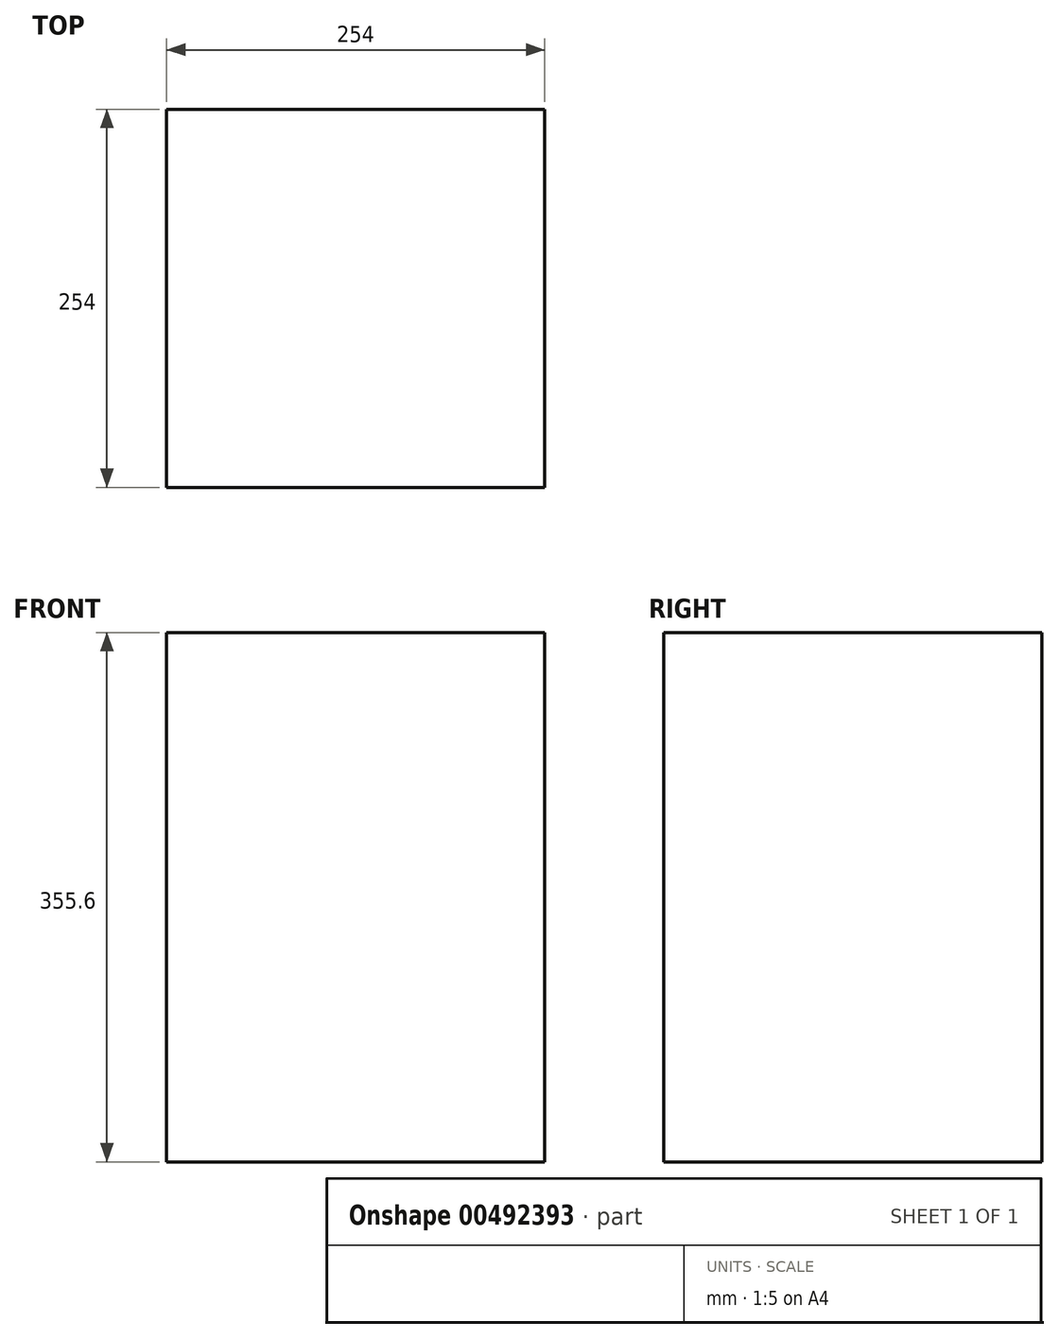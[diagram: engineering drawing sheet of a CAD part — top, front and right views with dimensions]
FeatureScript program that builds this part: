
annotation { "Feature Type Name" : "Feature", "Feature Type Description" : "" }
export const myFeature = defineFeature(function(context is Context, id is Id, definition is map)
    precondition{}
    {
        {
            var Q0;
            Q0=qCreatedBy(makeId("Top.planeOp"),FACE);
            var sketch = newSketch(context, id + "F0", { "sketchPlane" : qUnion([Q0])});
            skLineSegment(sketch, "E0.bottom", {"start": v(127, 127) * mm, "end": v(-127, 127) * mm});
            skLineSegment(sketch, "E0.top", {"start": v(127, -127) * mm, "end": v(-127, -127) * mm});
            skLineSegment(sketch, "E0.left", {"start": v(127, 127) * mm, "end": v(127, -127) * mm});
            skLineSegment(sketch, "E0.right", {"start": v(-127, 127) * mm, "end": v(-127, -127) * mm});
            skPoint(sketch, "E0.middle", {"position": v(0, 0) * mm});
            skSolve(sketch);
        }
        {
            var Q0;
            Q0=makeQuery(id+"F0.imprint","IMPRINT",FACE,{"disambiguationData":[TD([[makeQuery(id+"F0.imprint","IMPRINT",EDGE,{"derivedFrom":sQuery(id+"F0.wireOp",EDGE,"E0.bottom")}),1.0]])]});
            extrude(context, id + "F1", {"entities" : qUnion([Q0]), "depth" : 355.6 * mm});
        }
    });
